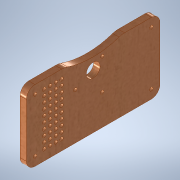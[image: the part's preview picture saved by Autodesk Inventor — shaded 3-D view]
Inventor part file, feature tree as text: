
AUTODESK INVENTOR PART (.ipt)
format: ipt  version: 2020.3 (Build 243373000, 373)  size: 235,008 bytes
history: native  units: mm
features: sketch x6, hole x4, extrude x2, fillet x2, other x1
ambient origin geometry x8: Origin, YZ Plane, XZ Plane, XY Plane, X Axis, Y Axis, Z Axis, Center Point
bodies: Body1 (feature_tree)
feature tree (15):
  other  "ソリッド1"
  extrude  "押し出し1"  Depth=61.5mm
  hole  "穴1"  [1 undecoded]
  fillet  "フィレット1"  Radius=5.5mm
  hole  "穴2"  [1 undecoded]
  hole  "穴3"  [1 undecoded]
  extrude  "押し出し2"  Depth=7.5mm
  fillet  "フィレット2"  Radius=7.5mm
  hole  "穴4"  [1 undecoded]
  sketch  "スケッチ1"
  sketch  "スケッチ2"
  sketch  "スケッチ3"
  sketch  "スケッチ4"
  sketch  "スケッチ5"
  sketch  "スケッチ6"
note: 4 required parameter values undecoded (feature->parameter linkage not recoverable at this tier; creation-order binding heuristic only, values carry confidence <= 0.55)
